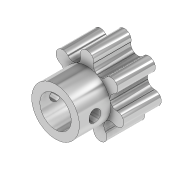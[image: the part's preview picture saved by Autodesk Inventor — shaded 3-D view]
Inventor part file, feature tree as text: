
AUTODESK INVENTOR PART (.ipt)
format: ipt  version: 2020 (Build 240168000, 168)  size: 219,648 bytes
history: native  units: in
note: dims shown in document units (in); Inventor stores cm internally (conversion verified against a paired STEP export)
features: extrude x3, sketch x3
ambient origin geometry x8: Origin, YZ Plane, XZ Plane, XY Plane, X Axis, Y Axis, Z Axis, Center Point
bodies: Solid1 (feature_tree)
feature tree (6):
  extrude  "Extrusion1"  Depth=0.1969in
  extrude  "Extrusion2"  Depth=0.084in
  extrude  "Extrusion3"  Depth=0.1969in
  sketch  "Sketch1"  dims[d0=0.1969in d1=0.4724in]
  sketch  "Sketch2"  dims[d2=0.0866in d5=0.084in]
  sketch  "Sketch3"  dims[d6=0.084in d7=0.084in d8=2.7559in d10=360.0deg d12=0.2362in d13=0.0in d14=0.1969in d15=0.0in d16=0.0748in d17=0.1575in d18=0.0in]
